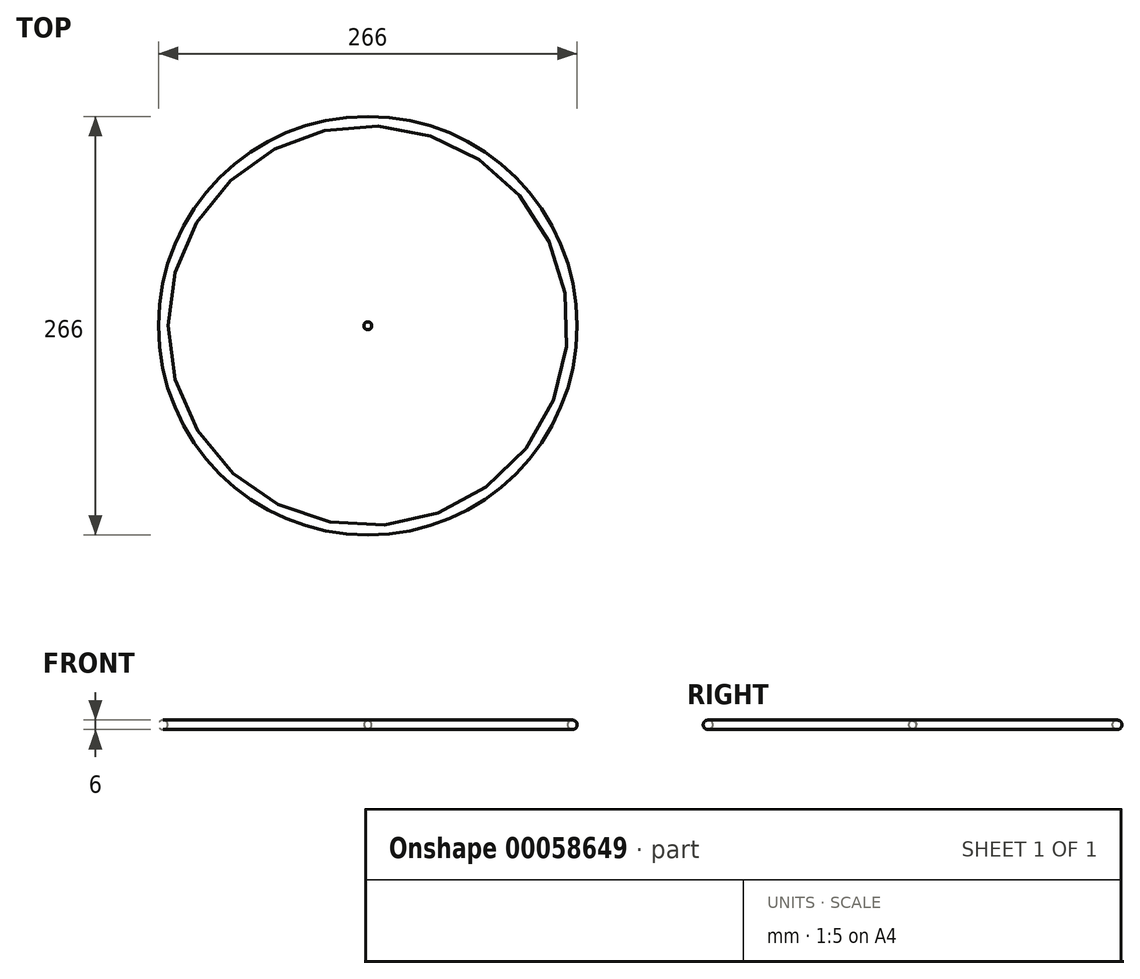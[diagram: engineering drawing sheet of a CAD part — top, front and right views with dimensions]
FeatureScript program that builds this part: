
annotation { "Feature Type Name" : "Feature", "Feature Type Description" : "" }
export const myFeature = defineFeature(function(context is Context, id is Id, definition is map)
    precondition{}
    {
        {
            var Q0;
            Q0=qCreatedBy(makeId("Top.planeOp"),FACE);
            var sketch = newSketch(context, id + "F0", { "sketchPlane" : qUnion([Q0])});
            skCircle(sketch, "E0", {"center": v(0, 0) * mm, "radius": 130 * mm});
            skCircle(sketch, "E1", {"center": v(0, 0) * mm, "radius": 2.96 * mm});
            skSolve(sketch);
        }
        {
            var Q0;
            Q0=qCreatedBy(makeId("Right.planeOp"),FACE);
            var sketch = newSketch(context, id + "F1", { "sketchPlane" : qUnion([Q0])});
            skCircle(sketch, "E2", {"center": v(-130, 0) * mm, "radius": 3 * mm});
            skSolve(sketch);
        }
        {
            var Q0;
            Q0=makeQuery(id+"F1.imprint","IMPRINT",FACE,{"disambiguationData":[TD([[makeQuery(id+"F1.imprint","IMPRINT",EDGE,{"derivedFrom":sQuery(id+"F1.wireOp",EDGE,"E2")}),1.0]])]});
            var Q1;
            Q1=sQuery(id+"F1.wireOp",EDGE,"E2");
            var Q2;
            Q2=sQuery(id+"F0.wireOp",EDGE,"E0");
            revolve(context, id + "F2", {"entities" : qUnion([Q0]), "surfaceEntities" : qUnion([Q1]), "axis" : qUnion([Q2]), "revolveType" : RevolveType.FULL});
        }
        {
            var Q0;
            Q0=qCreatedBy(makeId("Top.planeOp"),FACE);
            var sketch = newSketch(context, id + "F3", { "sketchPlane" : qUnion([Q0])});
            skPoint(sketch, "E3.rect.middle", {"position": v(0, 0) * mm});
            skArc(sketch, "E4", {"start": v(0, -2.5) * mm, "mid": v(2.51, 0) * mm, "end": v(0, 2.5) * mm});
            skLineSegment(sketch, "E5", {"start": v(0, -3.57) * mm, "end": v(0, 4.14) * mm});
            skSolve(sketch);
        }
        {
            var Q0;
            {var subQ1=sQuery(id+"F3.wireOp",EDGE,"E4");Q0=makeQuery(id+"F3.imprint","IMPRINT",FACE,{"disambiguationData":[TD([[makeQuery(id+"F3.imprint","IMPRINT",EDGE,{"derivedFrom":subQ1}),1.0]])]});}
            var Q1;
            Q1=sQuery(id+"F3.wireOp",EDGE,"E5");
            revolve(context, id + "F4", {"entities" : qUnion([Q0]), "axis" : qUnion([Q1]), "revolveType" : RevolveType.FULL});
        }
    });
